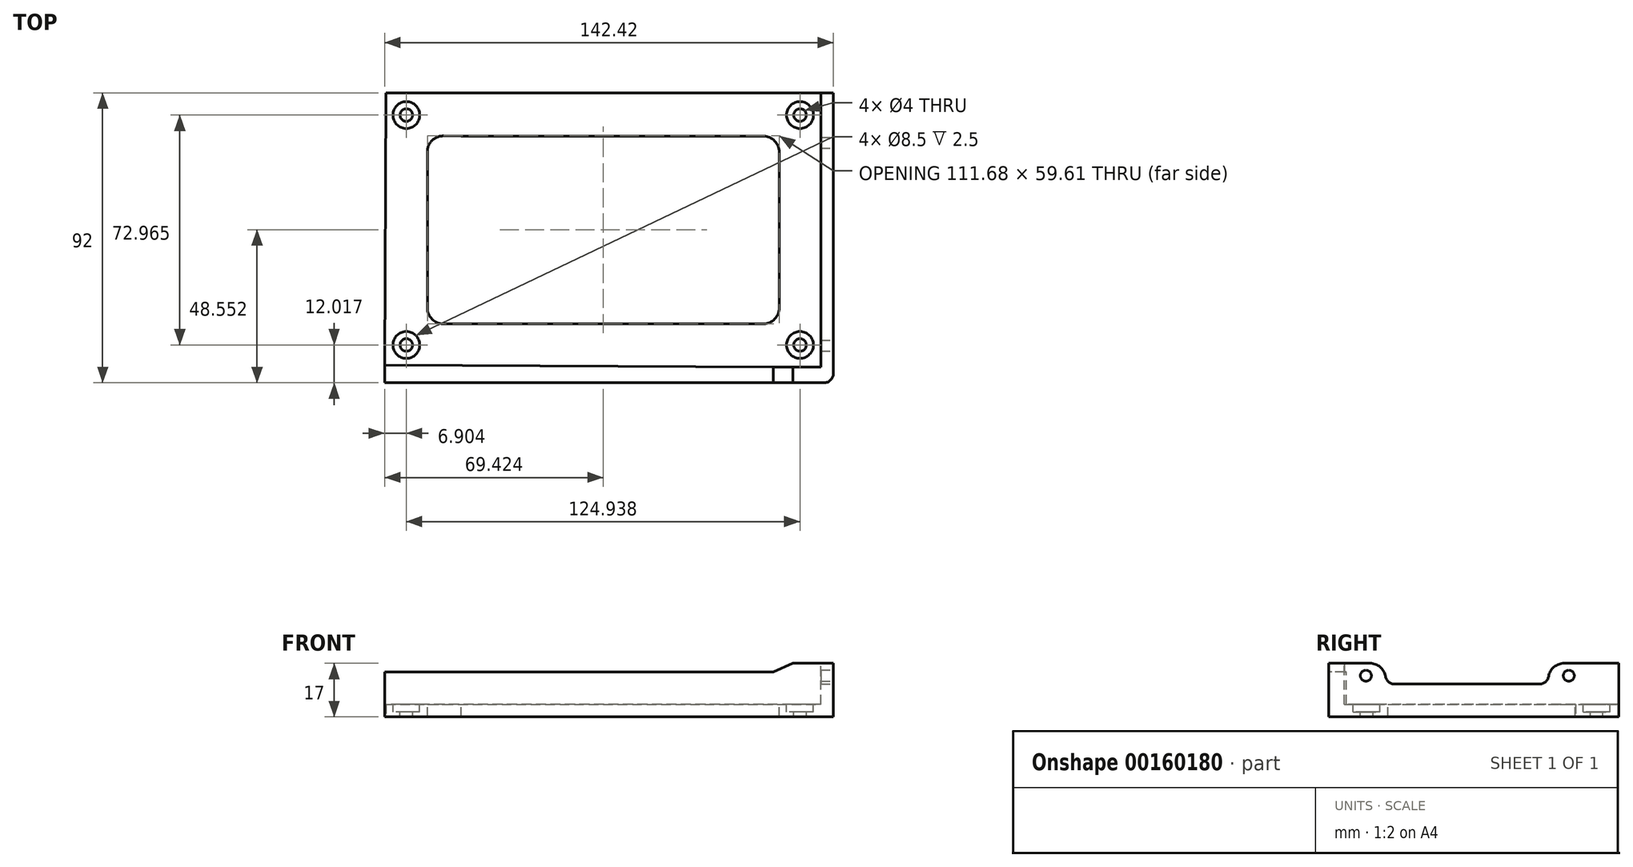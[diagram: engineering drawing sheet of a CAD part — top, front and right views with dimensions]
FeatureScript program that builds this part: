
annotation { "Feature Type Name" : "Feature", "Feature Type Description" : "" }
export const myFeature = defineFeature(function(context is Context, id is Id, definition is map)
    precondition{}
    {
        {
            var Q0;
            Q0=qCreatedBy(makeId("Top.planeOp"),FACE);
            var sketch = newSketch(context, id + "F0", { "sketchPlane" : qUnion([Q0])});
            skLineSegment(sketch, "E0", {"start": v(-74.36, 43.5) * mm, "end": v(67.64, 43.5) * mm});
            skLineSegment(sketch, "E1", {"start": v(67.64, 43.5) * mm, "end": v(67.64, -48.5) * mm});
            skLineSegment(sketch, "E2", {"start": v(67.64, -48.5) * mm, "end": v(-74.78, -48.5) * mm});
            skLineSegment(sketch, "E3", {"start": v(-74.78, -48.5) * mm, "end": v(-74.36, 43.5) * mm});
            skSolve(sketch);
        }
        {
            var Q0;
            Q0 = qSketchRegion(id + "F0", true);
            extrude(context, id + "F1", {"entities" : qUnion([Q0]), "depth" : 17 * mm});
        }
        {
            var Q0;
            Q0=makeQuery(id+"F1.opExtrude","CAP_FACE",FACE,{"disambiguationData":[OSD([sQuery(id+"F0.wireOp",EDGE,"E0"),sQuery(id+"F0.wireOp",EDGE,"E1"),sQuery(id+"F0.wireOp",EDGE,"E2"),sQuery(id+"F0.wireOp",EDGE,"E3")])],"isStart":false});
            var sketch = newSketch(context, id + "F2", { "sketchPlane" : qUnion([Q0])});
            skLineSegment(sketch, "E4", {"start": v(-74.36, 43.5) * mm, "end": v(63.64, 43.5) * mm});
            skLineSegment(sketch, "E5", {"start": v(63.64, 43.5) * mm, "end": v(63.64, -43.5) * mm});
            skLineSegment(sketch, "E6", {"start": v(63.64, -43.5) * mm, "end": v(-74.75, -42.87) * mm});
            skLineSegment(sketch, "E7", {"start": v(-74.75, -42.87) * mm, "end": v(-74.36, 43.5) * mm});
            skSolve(sketch);
        }
        {
            var Q0;
            Q0 = qSketchRegion(id + "F2", true);
            extrude(context, id + "F3", {"entities" : qUnion([Q0]), "operationType" : NewBodyOperationType.REMOVE, "oppositeDirection" : true, "depth" : 13 * mm});
        }
        {
            var Q0;
            Q0=makeQuery(id+"F1.opExtrude","SWEPT_FACE",FACE,{"disambiguationData":[OSD([sQuery(id+"F0.wireOp",EDGE,"E1")])]});
            var sketch = newSketch(context, id + "F4", { "sketchPlane" : qUnion([Q0])});
            skLineSegment(sketch, "E8", {"start": v(-36.8, 34.58) * mm, "end": v(-36.8, -27.83) * mm, "construction": true});
            skLineSegment(sketch, "E9", {"start": v(27.7, 34.58) * mm, "end": v(27.7, -27.83) * mm, "construction": true});
            skLineSegment(sketch, "E10", {"start": v(-53.44, 13) * mm, "end": v(52.3, 13) * mm, "construction": true});
            skSolve(sketch);
        }
        {
            var Q0;
            {var subQ0=sQuery(id+"F0.wireOp",EDGE,"E1");Q0=makeQuery(id+"F4.imprint","IMPRINT",FACE,{"disambiguationData":[TD([[makeQuery(id+"F4.imprint","IMPRINT",EDGE,{"derivedFrom":makeQuery(id+"F1.opExtrude","CAP_EDGE",EDGE,{"disambiguationData":[OSD([subQ0])],"isStart":true})}),-1.0]])]});}
            var sketch = newSketch(context, id + "F5", { "sketchPlane" : qUnion([Q0])});
            skLineSegment(sketch, "E11", {"start": v(-4.62, 9.06) * mm, "end": v(-4.62, 20.5) * mm, "construction": true});
            skLineSegment(sketch, "E12.left", {"start": v(6.65, 9.06) * mm, "end": v(6.65, 9.06) * mm});
            skLineSegment(sketch, "E12.right", {"start": v(-15.89, 9.06) * mm, "end": v(-15.89, 9.06) * mm});
            skPoint(sketch, "E12.middle", {"position": v(-4.62, 9.06) * mm});
            skLineSegment(sketch, "E13", {"start": v(47.55, 6.07) * mm, "end": v(-0.86, 6.04) * mm, "construction": true});
            skCircle(sketch, "E14", {"center": v(27.68, 13.06) * mm, "radius": 1.75 * mm});
            skCircle(sketch, "E15", {"center": v(-36.71, 13.06) * mm, "radius": 1.75 * mm});
            skArc(sketch, "E16", {"start": v(27.7, 17.06) * mm, "mid": v(27.68, 17.06) * mm, "end": v(27.66, 17.06) * mm});
            skLineSegment(sketch, "E17", {"start": v(-57.2, 16.39) * mm, "end": v(-57.02, 27.28) * mm});
            skLineSegment(sketch, "E18", {"start": v(-57.02, 27.28) * mm, "end": v(32.38, 26.98) * mm});
            skLineSegment(sketch, "E19", {"start": v(32.38, 26.98) * mm, "end": v(48.63, 26.18) * mm});
            skLineSegment(sketch, "E20", {"start": v(47.13, 17.75) * mm, "end": v(47.13, 17.06) * mm});
            skLineSegment(sketch, "E21", {"start": v(27.66, 17.06) * mm, "end": v(47.13, 17.06) * mm});
            skLineSegment(sketch, "E22.trimOffspring", {"start": v(-36.71, 17.06) * mm, "end": v(-57.2, 17.06) * mm});
            skLineSegment(sketch, "E23", {"start": v(47.13, 17.75) * mm, "end": v(48.63, 26.18) * mm});
            skPoint(sketch, "E24.orphan", {"position": v(-32.71, 13.06) * mm});
            skLineSegment(sketch, "E25", {"start": v(-30.44, 10.36) * mm, "end": v(21.2, 10.36) * mm});
            skLineSegment(sketch, "E26", {"start": v(-30.44, 10.36) * mm, "end": v(-30.44, 17.06) * mm});
            skLineSegment(sketch, "E27", {"start": v(-30.44, 17.06) * mm, "end": v(-36.71, 17.06) * mm});
            skLineSegment(sketch, "E28", {"start": v(21.2, 10.36) * mm, "end": v(21.2, 17.06) * mm});
            skLineSegment(sketch, "E29", {"start": v(21.2, 17.06) * mm, "end": v(27.7, 17.06) * mm});
            skSolve(sketch);
        }
        {
            var Q0;
            Q0 = qSketchRegion(id + "F5", true);
            extrude(context, id + "F6", {"entities" : qUnion([Q0]), "operationType" : NewBodyOperationType.REMOVE, "oppositeDirection" : true, "depth" : 7 * mm});
        }
        {
            var Q0;
            Q0=makeQuery(id+"F3.boolean.opBoolean","COPY",FACE,{"derivedFrom":makeQuery(id+"F3.opExtrude","CAP_FACE",FACE,{"disambiguationData":[OSD([sQuery(id+"F2.wireOp",EDGE,"E4"),sQuery(id+"F2.wireOp",EDGE,"E5"),sQuery(id+"F2.wireOp",EDGE,"E6"),sQuery(id+"F2.wireOp",EDGE,"E7")])],"isStart":false})});
            var sketch = newSketch(context, id + "F7", { "sketchPlane" : qUnion([Q0])});
            skLineSegment(sketch, "E30.bottom", {"start": v(50.48, -29.75) * mm, "end": v(-50.48, -29.75) * mm});
            skLineSegment(sketch, "E30.top", {"start": v(50.48, 29.75) * mm, "end": v(-50.48, 29.75) * mm});
            skLineSegment(sketch, "E30.left", {"start": v(50.48, -29.75) * mm, "end": v(50.48, 29.75) * mm});
            skPoint(sketch, "E30.middle", {"position": v(0, 0) * mm});
            skLineSegment(sketch, "E31", {"start": v(-50.48, -29.75) * mm, "end": v(-61.2, -29.75) * mm});
            skLineSegment(sketch, "E32", {"start": v(-61.2, -29.75) * mm, "end": v(-61.2, 29.95) * mm});
            skLineSegment(sketch, "E33", {"start": v(-61.2, 29.95) * mm, "end": v(-50.48, 29.75) * mm});
            skSolve(sketch);
        }
        {
            var Q0;
            Q0 = qSketchRegion(id + "F7", true);
            extrude(context, id + "F8", {"entities" : qUnion([Q0]), "operationType" : NewBodyOperationType.REMOVE, "oppositeDirection" : true, "depth" : 25 * mm});
        }
        {
            var Q0;
            Q0=makeQuery(id+"F1.opExtrude","SWEPT_EDGE",EDGE,{"disambiguationData":[OSD([sQuery(id+"F0.wireOp",EDGE,"E1"),sQuery(id+"F0.wireOp",EDGE,"E2")])]});
            var Q1;
            Q1=makeQuery(id+"F6.boolean.opBoolean","COPY",EDGE,{"derivedFrom":makeQuery(id+"F6.opExtrude","SWEPT_EDGE",EDGE,{"disambiguationData":[OSD([sQuery(id+"F5.wireOp",EDGE,"mKTJCFIW-7ouF-Ou2Z-ncZ1-uqUXdC0Cgj6g"),sQuery(id+"F5.wireOp",EDGE,"PHNWN93z-NXSl-PLL7-TCRB-mTlC7eGS1AN6")])]})});
            var Q2;
            Q2=makeQuery(id+"F6.boolean.opBoolean","COPY",EDGE,{"derivedFrom":makeQuery(id+"F6.opExtrude","SWEPT_EDGE",EDGE,{"disambiguationData":[OSD([sQuery(id+"F5.wireOp",EDGE,"Ow2x9tDx-N52T-hukb-mBo4-eDX645Dk5Jdt"),sQuery(id+"F5.wireOp",EDGE,"WzHWg2Zl-bjKV-ZBuv-FoIn-cCbKl3M08u3X")])]})});
            fillet(context, id + "F9", {"entities" : qUnion([Q0, Q1, Q2]), "radius" : 3 * mm, "tangentPropagation" : true, "allowEdgeOverflow" : false});
        }
        {
            var Q0;
            Q0=makeQuery(id+"F8.boolean.opBoolean","COPY",EDGE,{"derivedFrom":makeQuery(id+"F8.opExtrude","SWEPT_EDGE",EDGE,{"disambiguationData":[OSD([sQuery(id+"F7.wireOp",EDGE,"E30.top"),sQuery(id+"F7.wireOp",EDGE,"E30.left")])]})});
            var Q1;
            Q1=makeQuery(id+"F8.boolean.opBoolean","COPY",EDGE,{"derivedFrom":makeQuery(id+"F8.opExtrude","SWEPT_EDGE",EDGE,{"disambiguationData":[OSD([sQuery(id+"F7.wireOp",EDGE,"E32"),sQuery(id+"F7.wireOp",EDGE,"E33")])]})});
            var Q2;
            Q2=makeQuery(id+"F8.boolean.opBoolean","COPY",EDGE,{"derivedFrom":makeQuery(id+"F8.opExtrude","SWEPT_EDGE",EDGE,{"disambiguationData":[OSD([sQuery(id+"F7.wireOp",EDGE,"E30.bottom"),sQuery(id+"F7.wireOp",EDGE,"E30.left")])]})});
            var Q3;
            Q3=makeQuery(id+"F8.boolean.opBoolean","COPY",EDGE,{"derivedFrom":makeQuery(id+"F8.opExtrude","SWEPT_EDGE",EDGE,{"disambiguationData":[OSD([sQuery(id+"F7.wireOp",EDGE,"E31"),sQuery(id+"F7.wireOp",EDGE,"E32")])]})});
            fillet(context, id + "F10", {"entities" : qUnion([Q0, Q1, Q2, Q3]), "radius" : 5 * mm, "tangentPropagation" : true, "allowEdgeOverflow" : false});
        }
        {
            var Q0;
            Q0=makeQuery(id+"F3.boolean.opBoolean","COPY",FACE,{"derivedFrom":makeQuery(id+"F3.opExtrude","CAP_FACE",FACE,{"disambiguationData":[OSD([sQuery(id+"F2.wireOp",EDGE,"E4"),sQuery(id+"F2.wireOp",EDGE,"E5"),sQuery(id+"F2.wireOp",EDGE,"E6"),sQuery(id+"F2.wireOp",EDGE,"E7")])],"isStart":false})});
            var sketch = newSketch(context, id + "F11", { "sketchPlane" : qUnion([Q0])});
            skPoint(sketch, "E34.startSnap0", {"position": v(0, 36.63) * mm});
            skPoint(sketch, "E35.orphan", {"position": v(0, 43.5) * mm});
            skPoint(sketch, "E36.end.orphan", {"position": v(0, 29.75) * mm});
            skPoint(sketch, "E37.endSnap0", {"position": v(0, -36.48) * mm});
            skLineSegment(sketch, "E38", {"start": v(-69.88, -36.48) * mm, "end": v(-65.88, -36.48) * mm, "construction": true});
            skCircle(sketch, "E39", {"center": v(-67.88, -36.48) * mm, "radius": 2 * mm});
            skCircle(sketch, "E40", {"center": v(57.06, -36.48) * mm, "radius": 2 * mm});
            skLineSegment(sketch, "E41.trimOffspring", {"start": v(57.06, -34.48) * mm, "end": v(57.06, -38.48) * mm, "construction": true});
            skLineSegment(sketch, "E42.trimOffspring", {"start": v(-67.88, -34.48) * mm, "end": v(-67.88, -38.48) * mm, "construction": true});
            skPoint(sketch, "E43.orphan", {"position": v(-72.61, 36.63) * mm});
            skLineSegment(sketch, "E44.trimOffspring", {"start": v(55.06, -36.48) * mm, "end": v(59.06, -36.48) * mm, "construction": true});
            skPoint(sketch, "E45.orphan", {"position": v(-71.82, -36.48) * mm});
            skCircle(sketch, "E46.MirrorC", {"center": v(-67.88, 36.48) * mm, "radius": 2 * mm});
            skCircle(sketch, "E47.MirrorC", {"center": v(57.06, 36.48) * mm, "radius": 2 * mm});
            skSolve(sketch);
        }
        {
            var Q0;
            Q0 = qSketchRegion(id + "F11", true);
            extrude(context, id + "F12", {"entities" : qUnion([Q0]), "operationType" : NewBodyOperationType.REMOVE, "oppositeDirection" : true, "depth" : 25 * mm});
        }
        {
            var Q0;
            Q0=makeQuery(id+"F3.boolean.opBoolean","COPY",FACE,{"derivedFrom":makeQuery(id+"F3.opExtrude","CAP_FACE",FACE,{"disambiguationData":[OSD([sQuery(id+"F2.wireOp",EDGE,"E4"),sQuery(id+"F2.wireOp",EDGE,"E5"),sQuery(id+"F2.wireOp",EDGE,"E6"),sQuery(id+"F2.wireOp",EDGE,"E7")])],"isStart":false})});
            var sketch = newSketch(context, id + "F13", { "sketchPlane" : qUnion([Q0])});
            skCircle(sketch, "E48", {"center": v(-67.88, 36.48) * mm, "radius": 4.25 * mm});
            skCircle(sketch, "E49", {"center": v(57.06, 36.48) * mm, "radius": 4.25 * mm});
            skCircle(sketch, "E50.MirrorC", {"center": v(-67.88, -36.48) * mm, "radius": 4.25 * mm});
            skCircle(sketch, "E51.MirrorC", {"center": v(57.06, -36.48) * mm, "radius": 4.25 * mm});
            skSolve(sketch);
        }
        {
            var Q0;
            Q0 = qSketchRegion(id + "F13", true);
            extrude(context, id + "F14", {"entities" : qUnion([Q0]), "operationType" : NewBodyOperationType.REMOVE, "oppositeDirection" : true, "depth" : 2.5 * mm});
        }
        {
            var Q0;
            Q0=makeQuery(id+"F1.opExtrude","SWEPT_FACE",FACE,{"disambiguationData":[OSD([sQuery(id+"F0.wireOp",EDGE,"E2")])]});
            var sketch = newSketch(context, id + "F15", { "sketchPlane" : qUnion([Q0])});
            skLineSegment(sketch, "E52", {"start": v(-78.4, 14.23) * mm, "end": v(-78.4, 22.23) * mm});
            skLineSegment(sketch, "E53", {"start": v(-78.4, 22.23) * mm, "end": v(48, 22.23) * mm});
            skLineSegment(sketch, "E54", {"start": v(48, 22.23) * mm, "end": v(54.8, 17) * mm});
            skLineSegment(sketch, "E55", {"start": v(54.8, 17) * mm, "end": v(48.52, 14.23) * mm});
            skLineSegment(sketch, "E56", {"start": v(-78.4, 14.23) * mm, "end": v(48.52, 14.23) * mm});
            skSolve(sketch);
        }
        {
            var Q0;
            Q0 = qSketchRegion(id + "F15", true);
            extrude(context, id + "F16", {"entities" : qUnion([Q0]), "operationType" : NewBodyOperationType.REMOVE, "oppositeDirection" : true, "depth" : 25 * mm});
        }
        {
            var Q0;
            Q0=makeQuery(id+"F6.boolean.opBoolean","INTERSECT",EDGE,{"derivedFrom":[makeQuery(id+"F1.opExtrude","CAP_FACE",FACE,{"disambiguationData":[OSD([sQuery(id+"F0.wireOp",EDGE,"E0"),sQuery(id+"F0.wireOp",EDGE,"E1"),sQuery(id+"F0.wireOp",EDGE,"E2"),sQuery(id+"F0.wireOp",EDGE,"E3")])],"isStart":false}),makeQuery(id+"F6.opExtrude","SWEPT_FACE",FACE,{"disambiguationData":[OSD([sQuery(id+"F5.wireOp",EDGE,"E26")])]})]});
            var Q1;
            Q1=makeQuery(id+"F6.boolean.opBoolean","INTERSECT",EDGE,{"derivedFrom":[makeQuery(id+"F1.opExtrude","CAP_FACE",FACE,{"disambiguationData":[OSD([sQuery(id+"F0.wireOp",EDGE,"E0"),sQuery(id+"F0.wireOp",EDGE,"E1"),sQuery(id+"F0.wireOp",EDGE,"E2"),sQuery(id+"F0.wireOp",EDGE,"E3")])],"isStart":false}),makeQuery(id+"F6.opExtrude","SWEPT_FACE",FACE,{"disambiguationData":[OSD([sQuery(id+"F5.wireOp",EDGE,"E28")])]})]});
            fillet(context, id + "F17", {"entities" : qUnion([Q0, Q1]), "radius" : 5 * mm, "tangentPropagation" : true, "allowEdgeOverflow" : false});
        }
        {
            var Q0;
            Q0=makeQuery(id+"F6.boolean.opBoolean","COPY",EDGE,{"derivedFrom":makeQuery(id+"F6.opExtrude","SWEPT_EDGE",EDGE,{"disambiguationData":[OSD([sQuery(id+"F5.wireOp",EDGE,"E25"),sQuery(id+"F5.wireOp",EDGE,"E26")])]})});
            var Q1;
            Q1=makeQuery(id+"F6.boolean.opBoolean","COPY",EDGE,{"derivedFrom":makeQuery(id+"F6.opExtrude","SWEPT_EDGE",EDGE,{"disambiguationData":[OSD([sQuery(id+"F5.wireOp",EDGE,"E25"),sQuery(id+"F5.wireOp",EDGE,"E28")])]})});
            fillet(context, id + "F18", {"entities" : qUnion([Q0, Q1]), "radius" : 3 * mm, "tangentPropagation" : true, "allowEdgeOverflow" : false});
        }
    });
